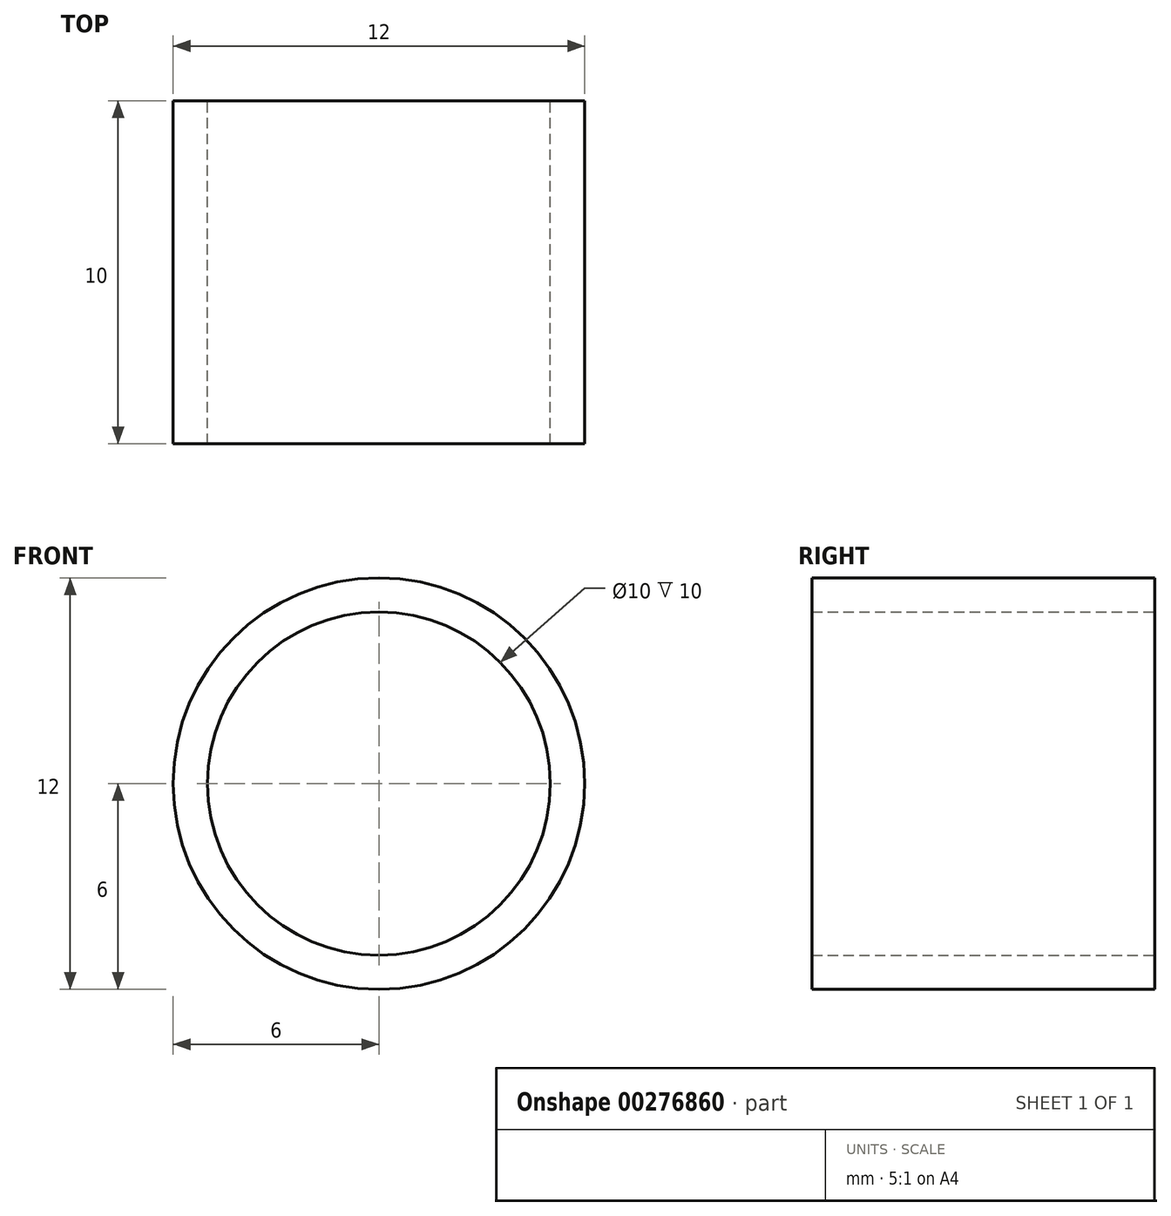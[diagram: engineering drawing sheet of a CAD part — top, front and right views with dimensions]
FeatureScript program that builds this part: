
annotation { "Feature Type Name" : "Feature", "Feature Type Description" : "" }
export const myFeature = defineFeature(function(context is Context, id is Id, definition is map)
    precondition{}
    {
        {
            var Q0;
            Q0=qCreatedBy(makeId("Front.planeOp"),FACE);
            var sketch = newSketch(context, id + "F0", { "sketchPlane" : qUnion([Q0])});
            skCircle(sketch, "E0", {"center": v(0, 0) * mm, "radius": 6 * mm});
            skCircle(sketch, "E1", {"center": v(0, 0) * mm, "radius": 5 * mm});
            skSolve(sketch);
        }
        {
            var Q0;
            Q0=makeQuery(id+"F0.imprint","IMPRINT",FACE,{"disambiguationData":[TD([[makeQuery(id+"F0.imprint","IMPRINT",EDGE,{"derivedFrom":sQuery(id+"F0.wireOp",EDGE,"E0")}),1.0]])]});
            extrude(context, id + "F1", {"entities" : qUnion([Q0]), "depth" : 10 * mm});
        }
    });
